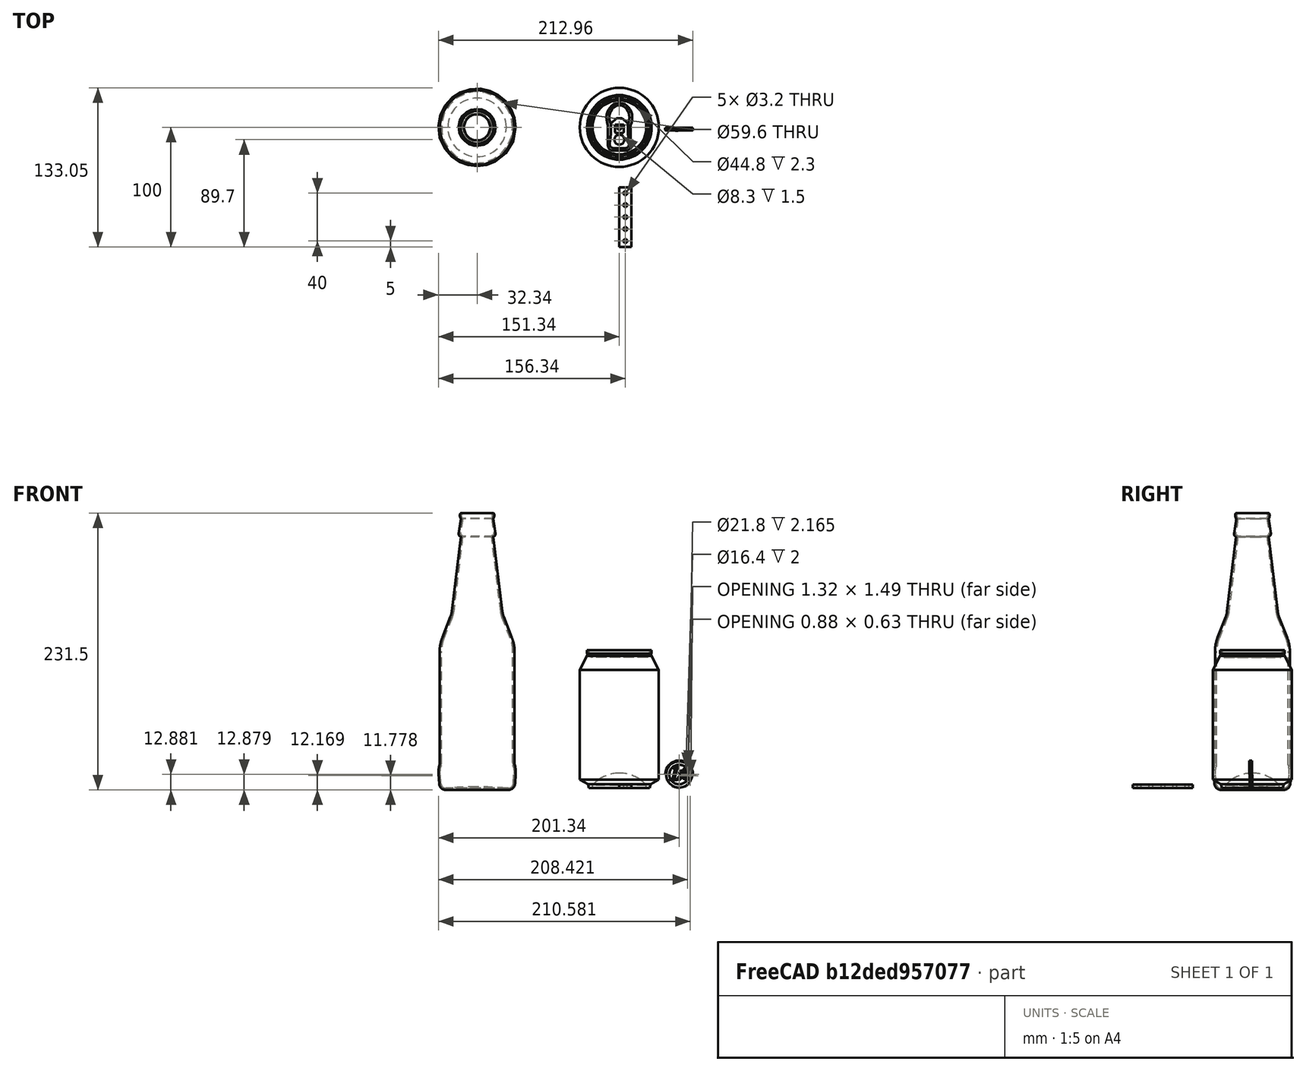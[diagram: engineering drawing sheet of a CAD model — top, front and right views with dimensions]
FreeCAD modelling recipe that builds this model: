
FCSTD DOCUMENT  (FreeCAD 0.20R29410 (Git))
Label: Mecano
License: All rights reserved
LicenseURL: http://en.wikipedia.org/wiki/All_rights_reserved
objects: Part::Cylinder×5, Part::Feature×3, Part::Box×1, Part::MultiFuse×1, Part::Cut×1
note: 11 computed .brp shape members not serialized (recipe doc carries the construction recipe); baked Part::Feature solids carry a one-line shape summary decoded from their .brp

FEATURE [Part::Feature] Compound001  label="Euro-coin"
  Placement = pos=(50,99.808,10.9983) rot=(1,0,0;1.58825rad)
  shape: bbox 23.25 x 2.737 x 23.28 mm, 903 faces, 22 solids (baked)
FEATURE [Part::Feature] Thickness001  label="Bottle"
  Placement = pos=(-119,100,0) rot=(0,0,1;0rad)
  shape: bbox 71.75 x 74.3 x 235 mm, 40 faces (baked)
FEATURE [Part::Feature] Fusion001  label="Can"
  Placement = pos=(0,100,0) rot=(0,0,1;0rad)
  shape: bbox 66.1 x 66.1 x 115.2 mm, 53 faces (baked)
FEATURE [Part::Box] Box  label="Cubo"
  AttacherType = Attacher::AttachEngine3D
  Height = 3
  Length = 10
  Width = 50
FEATURE [Part::Cylinder] Cylinder  label="Cilindro"
  Angle = 360
  AttacherType = Attacher::AttachEngine3D
  FirstAngle = 0
  Height = 10
  Placement = pos=(5,5,-3) rot=(0,0,1;0rad)
  Radius = 1.6
  SecondAngle = 0
FEATURE [Part::Cylinder] Cylinder001  label="Cilindro001"
  Angle = 360
  AttacherType = Attacher::AttachEngine3D
  FirstAngle = 0
  Height = 10
  Placement = pos=(5,15,-3) rot=(0,0,1;0rad)
  Radius = 1.6
  SecondAngle = 0
FEATURE [Part::Cylinder] Cylinder002  label="Cilindro002"
  Angle = 360
  AttacherType = Attacher::AttachEngine3D
  FirstAngle = 0
  Height = 10
  Placement = pos=(5,25,-3) rot=(0,0,1;0rad)
  Radius = 1.6
  SecondAngle = 0
FEATURE [Part::Cylinder] Cylinder003  label="Cilindro003"
  Angle = 360
  AttacherType = Attacher::AttachEngine3D
  FirstAngle = 0
  Height = 10
  Placement = pos=(5,35,-3) rot=(0,0,1;0rad)
  Radius = 1.6
  SecondAngle = 0
FEATURE [Part::Cylinder] Cylinder004  label="Cilindro004"
  Angle = 360
  AttacherType = Attacher::AttachEngine3D
  FirstAngle = 0
  Height = 10
  Placement = pos=(5,45,-3) rot=(0,0,1;0rad)
  Radius = 1.6
  SecondAngle = 0
FEATURE [Part::MultiFuse] Fusion
  Shapes = -> [Cylinder,Cylinder001,Cylinder002,Cylinder003,Cylinder004]
FEATURE [Part::Cut] Cut
  Base = -> Box
  Tool = -> Fusion
